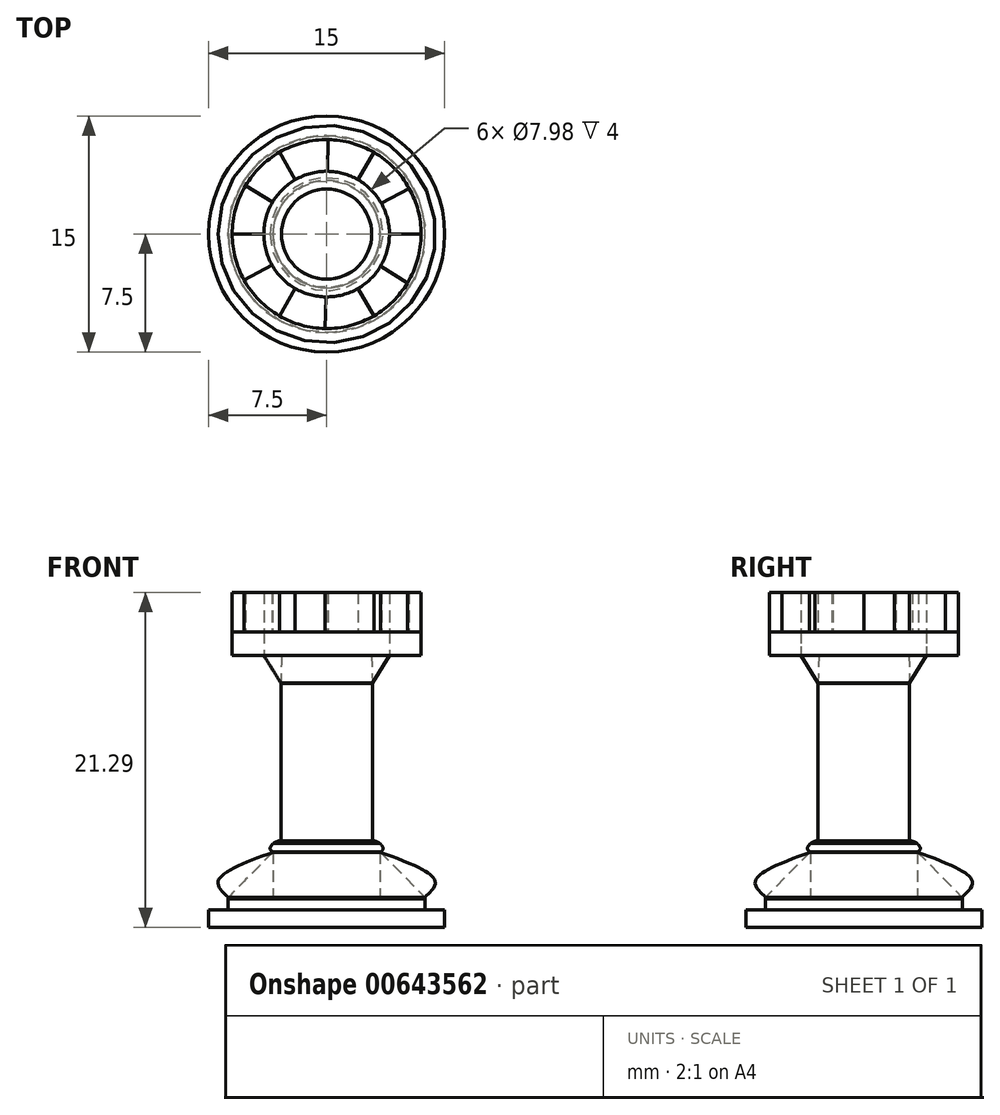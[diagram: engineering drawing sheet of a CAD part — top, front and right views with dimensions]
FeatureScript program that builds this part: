
annotation { "Feature Type Name" : "Feature", "Feature Type Description" : "" }
export const myFeature = defineFeature(function(context is Context, id is Id, definition is map)
    precondition{}
    {
        {
            var Q0;
            Q0=qCreatedBy(makeId("Top.planeOp"),FACE);
            var sketch = newSketch(context, id + "F0", { "sketchPlane" : qUnion([Q0])});
            skCircle(sketch, "E0", {"center": v(0, 0) * mm, "radius": 7.5 * mm});
            skSolve(sketch);
        }
        {
            var Q0;
            Q0=makeQuery(id+"F0.imprint","IMPRINT",FACE,{"disambiguationData":[TD([[makeQuery(id+"F0.imprint","IMPRINT",EDGE,{"derivedFrom":sQuery(id+"F0.wireOp",EDGE,"E0")}),1.0]])]});
            extrude(context, id + "F1", {"entities" : qUnion([Q0]), "depth" : 1.11 * mm, "offsetDistance" : 25 * mm});
        }
        {
            var Q0;
            Q0=makeQuery(id+"F1.opExtrude","CAP_FACE",FACE,{"disambiguationData":[OSD([sQuery(id+"F0.wireOp",EDGE,"E0")])],"isStart":false});
            var sketch = newSketch(context, id + "F2", { "sketchPlane" : qUnion([Q0])});
            skCircle(sketch, "E1", {"center": v(0, 0) * mm, "radius": 6.25 * mm});
            skSolve(sketch);
        }
        {
            var Q0;
            Q0=makeQuery(id+"F2.imprint","IMPRINT",FACE,{"disambiguationData":[TD([[makeQuery(id+"F2.imprint","IMPRINT",EDGE,{"derivedFrom":sQuery(id+"F2.wireOp",EDGE,"E1")}),1.0]])]});
            extrude(context, id + "F3", {"entities" : qUnion([Q0]), "operationType" : NewBodyOperationType.ADD, "depth" : 0.7 * mm, "offsetDistance" : 25 * mm});
        }
        {
            var Q0;
            Q0=qCreatedBy(makeId("Front.planeOp"),FACE);
            var sketch = newSketch(context, id + "F4", { "sketchPlane" : qUnion([Q0])});
            skLineSegment(sketch, "E2", {"start": v(-6.24, 1.92) * mm, "end": v(-3.41, 4.78) * mm});
            skFitSpline(sketch, "E3", {"points": [v(-6.24, 1.92) * mm, v(-6.9, 2.94) * mm, v(-3.41, 4.78) * mm], "startDerivative": vector(-3.13, 2.85) * mm, "endDerivative": vector(7.75, 2.86) * mm});
            skFitSpline(sketch, "E4", {"points": [v(-3.41, 4.78) * mm, v(-2.66, 5.77) * mm, v(-2.53, 6.42) * mm, v(-2.53, 6.45) * mm], "startDerivative": vector(1.73, 1.75) * mm, "endDerivative": vector(-0.01, 0.26) * mm});
            skSolve(sketch);
        }
        {
            var Q0;
            Q0=makeQuery(id+"F4.imprint","IMPRINT",FACE,{"disambiguationData":[TD([[makeQuery(id+"F4.imprint","IMPRINT",EDGE,{"derivedFrom":sQuery(id+"F4.wireOp",EDGE,"E2")}),1.0]])]});
            var Q1;
            Q1=makeQuery(id+"F3.opExtrude","CAP_EDGE",EDGE,{"disambiguationData":[OSD([sQuery(id+"F2.wireOp",EDGE,"E1")])],"isStart":false});
            revolve(context, id + "F5", {"entities" : qUnion([Q0]), "axis" : qUnion([Q1]), "revolveType" : RevolveType.FULL});
        }
        {
            var Q0;
            Q0=qCreatedBy(makeId("Top.planeOp"),FACE);
            var sketch = newSketch(context, id + "F6", { "sketchPlane" : qUnion([Q0])});
            skCircle(sketch, "E5", {"center": v(0, 0) * mm, "radius": 3.4 * mm});
            skSolve(sketch);
        }
        {
            var Q0;
            Q0 = qSketchRegion(id + "F6", true);
            extrude(context, id + "F7", {"entities" : qUnion([Q0]), "operationType" : NewBodyOperationType.ADD, "depth" : 5.5 * mm, "offsetDistance" : 25 * mm});
        }
        {
            var Q0;
            Q0=qCreatedBy(makeId("Front.planeOp"),FACE);
            var sketch = newSketch(context, id + "F8", { "sketchPlane" : qUnion([Q0])});
            skLineSegment(sketch, "E6", {"start": v(-6.24, 1.92) * mm, "end": v(-6.25, 1.81) * mm});
            skArc(sketch, "E7", {"start": v(-6.24, 1.92) * mm, "mid": v(-6.26, 1.87) * mm, "end": v(-6.25, 1.81) * mm});
            skSolve(sketch);
        }
        {
            var Q0;
            Q0 = qSketchRegion(id + "F8", true);
            var Q1;
            Q1=makeQuery(id+"F3.opExtrude","CAP_EDGE",EDGE,{"disambiguationData":[OSD([sQuery(id+"F2.wireOp",EDGE,"E1")])],"isStart":false});
            revolve(context, id + "F9", {"entities" : qUnion([Q0]), "axis" : qUnion([Q1]), "revolveType" : RevolveType.FULL});
        }
        {
            var Q0;
            Q0=qCreatedBy(makeId("Front.planeOp"),FACE);
            var sketch = newSketch(context, id + "F10", { "sketchPlane" : qUnion([Q0])});
            skFitSpline(sketch, "E8", {"points": [v(-3.4, 4.79) * mm, v(-3.6, 5) * mm, v(-3.4, 5.33) * mm], "startDerivative": vector(-0.58, 0.42) * mm, "endDerivative": vector(0.56, 0.65) * mm});
            skLineSegment(sketch, "E9", {"start": v(-3.4, 5.33) * mm, "end": v(-3.4, 4.79) * mm});
            skSolve(sketch);
        }
        {
            var Q0;
            Q0=makeQuery(id+"F10.imprint","IMPRINT",FACE,{"disambiguationData":[TD([[makeQuery(id+"F10.imprint","IMPRINT",EDGE,{"derivedFrom":sQuery(id+"F10.wireOp",EDGE,"E8")}),-1.0]])]});
            var Q1;
            Q1=makeQuery(id+"F7.opExtrude","CAP_EDGE",EDGE,{"disambiguationData":[OSD([sQuery(id+"F6.wireOp",EDGE,"E5")])],"isStart":false});
            revolve(context, id + "F11", {"operationType" : NewBodyOperationType.ADD, "entities" : qUnion([Q0]), "axis" : qUnion([Q1]), "revolveType" : RevolveType.FULL});
        }
        {
            var Q0;
            Q0=makeQuery(id+"F7.opExtrude","CAP_EDGE",EDGE,{"disambiguationData":[OSD([sQuery(id+"F6.wireOp",EDGE,"E5")])],"isStart":false});
            fillet(context, id + "F12", {"entities" : qUnion([Q0]), "radius" : 0.8 * mm, "tangentPropagation" : true, "allowEdgeOverflow" : false});
        }
        {
            var Q0;
            Q0=makeQuery(id+"F7.opExtrude","CAP_FACE",FACE,{"disambiguationData":[OSD([sQuery(id+"F6.wireOp",EDGE,"E5")])],"isStart":false});
            extrude(context, id + "F13", {"entities" : qUnion([Q0]), "operationType" : NewBodyOperationType.ADD, "depth" : 10 * mm, "offsetDistance" : 25 * mm});
        }
        {
            var Q0;
            Q0=makeQuery(id+"F13.opExtrude","CAP_FACE",FACE,{"disambiguationData":[OSD([sQuery(id+"F6.wireOp",EDGE,"E5")])],"isStart":false});
            var sketch = newSketch(context, id + "F14", { "sketchPlane" : qUnion([Q0])});
            skCircle(sketch, "E10", {"center": v(0, 0) * mm, "radius": 2.9 * mm});
            skSolve(sketch);
        }
        {
            var Q0;
            Q0=qCreatedBy(makeId("Right.planeOp"),FACE);
            var sketch = newSketch(context, id + "F15", { "sketchPlane" : qUnion([Q0])});
            skLineSegment(sketch, "E11", {"start": v(2.9, 15.53) * mm, "end": v(3.99, 17.29) * mm});
            skLineSegment(sketch, "E12", {"start": v(3.99, 17.29) * mm, "end": v(2.86, 17.29) * mm});
            skLineSegment(sketch, "E13", {"start": v(2.86, 17.29) * mm, "end": v(2.9, 15.53) * mm});
            skSolve(sketch);
        }
        {
            var Q0;
            Q0 = qSketchRegion(id + "F15", true);
            var Q1;
            Q1=sQuery(id+"F14.wireOp",EDGE,"E10");
            revolve(context, id + "F16", {"entities" : qUnion([Q0]), "axis" : qUnion([Q1]), "revolveType" : RevolveType.FULL});
        }
        {
            var Q0;
            Q0=makeQuery(id+"F16.opRevolve","SWEPT_FACE",FACE,{"disambiguationData":[OSD([sQuery(id+"F15.wireOp",EDGE,"E12")])]});
            var sketch = newSketch(context, id + "F17", { "sketchPlane" : qUnion([Q0])});
            skCircle(sketch, "E14", {"center": v(0, 0) * mm, "radius": 6 * mm});
            skSolve(sketch);
        }
        {
            var Q0;
            Q0=makeQuery(id+"F17.imprint","IMPRINT",FACE,{"disambiguationData":[TD([[makeQuery(id+"F17.imprint","IMPRINT",EDGE,{"derivedFrom":sQuery(id+"F17.wireOp",EDGE,"E14")}),1.0]])]});
            extrude(context, id + "F18", {"entities" : qUnion([Q0]), "depth" : 1.5 * mm, "offsetDistance" : 25 * mm});
        }
        {
            var Q0;
            Q0=makeQuery(id+"F18.opExtrude","CAP_FACE",FACE,{"disambiguationData":[OSD([sQuery(id+"F15.wireOp",EDGE,"E11"),sQuery(id+"F15.wireOp",EDGE,"E12"),sQuery(id+"F17.wireOp",EDGE,"E14")])],"isStart":false});
            var sketch = newSketch(context, id + "F19", { "sketchPlane" : qUnion([Q0])});
            skLineSegment(sketch, "E15", {"start": v(-6, 0) * mm, "end": v(-3.99, 0) * mm});
            skLineSegment(sketch, "E16", {"start": v(-5.14, 3.1) * mm, "end": v(-3.43, 2.03) * mm});
            skSolve(sketch);
        }
        {
            var Q0;
            {var subQ0=sQuery(id+"F19.wireOp",EDGE,"E15");Q0=makeQuery(id+"F19.imprint","IMPRINT",FACE,{"disambiguationData":[TD([[makeQuery(id+"F19.imprint","IMPRINT",EDGE,{"derivedFrom":subQ0}),1.0]])]});}
            extrude(context, id + "F20", {"entities" : qUnion([Q0]), "operationType" : NewBodyOperationType.ADD, "depth" : 2.5 * mm, "offsetDistance" : 25 * mm});
        }
        {
            var Q0;
            Q0=makeQuery(id+"F18.opExtrude","SWEPT_BODY",BODY,{"disambiguationData":[OSD([sQuery(id+"F15.wireOp",EDGE,"E11"),sQuery(id+"F15.wireOp",EDGE,"E12"),sQuery(id+"F17.wireOp",EDGE,"E14")])]});
            var Q1;
            {var subQ0=sQuery(id+"F15.wireOp",EDGE,"E12");var subQ1=sQuery(id+"F15.wireOp",EDGE,"E11");Q1=makeQuery(id+"F20.boolean.opBoolean","MERGE",FACE,{"derivedFrom":[makeQuery(id+"F18.opExtrude","SWEPT_FACE",FACE,{"disambiguationData":[OSD([subQ1,subQ0])]}),makeQuery(id+"F20.opExtrude","SWEPT_FACE",FACE,{"disambiguationData":[OSD([subQ1,subQ0])]})]});}
            circularPattern(context, id + "F21", {"entities" : qUnion([Q0]), "axis" : qUnion([Q1]), "angle" : 360 * degree, "instanceCount" : 6, "equalSpace" : true});
        }
    });
